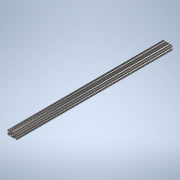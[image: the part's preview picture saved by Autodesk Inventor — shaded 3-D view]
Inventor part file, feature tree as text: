
AUTODESK INVENTOR PART (.ipt)
format: ipt  version: 2020 (Build 240168000, 168)  size: 360,448 bytes
history: native  units: in
note: dims shown in document units (in); Inventor stores cm internally (conversion verified against a paired STEP export)
features: sketch x2, extrude x1
ambient origin geometry x8: Origin, YZ Plane, XZ Plane, XY Plane, X Axis, Y Axis, Z Axis, Center Point
bodies: Solid1 (feature_tree)
feature tree (3):
  extrude  "Extrusion1"  [1 undecoded]
  sketch  "Sketch2"
  sketch  "Sketch1"  dims[d0=33.0in d1=0.0in]
note: 1 required parameter value undecoded (feature->parameter linkage not recoverable at this tier; creation-order binding heuristic only, values carry confidence <= 0.55)
